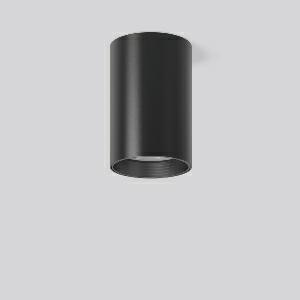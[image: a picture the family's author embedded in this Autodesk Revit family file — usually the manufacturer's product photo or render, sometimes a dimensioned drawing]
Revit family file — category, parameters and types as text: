
# Revit family: heledon_maxi_a_931227_003_1_ba15
name_source: partatom
category: Lighting Fixtures
units: mm (PartAtom-declared; Revit-internal decimal feet)

## family parameters
Cut with Voids When Loaded = No
Host = Face
Light Source = No
Part Type = Normal
Room Calculation Point = No
Round Connector Dimension = Use Diameter
Shared = No

## types (1)
- HELEDON maxi A (1 x LED Modul 940, 3900 lm, 4000)
    Apparent Load = 35 VA
    Approval mark = CE
    CIE Flux Codes = 97 100 100 100 100
    Color Rendering = 92
    Color Temperature = 4000
    Default Elevation = 1800 mm
    Description = Series: HELEDON maxi
Cylindrical surface-mounted downlight. Housing: die-cast aluminium, powder-coated. Internal ceiling frame polycarbonate with bayonet mounting. Black plastic ring and recessed LED to prevent glare from the side. Optical assembly with lens made of plastic (polycarbonate) for the best homogeneous light distribution - can be changed without tools. Best colour rendering index Ra>90. Suitable for Ceiling mounting. Easy installation with a separate ceiling frame with bayonet mounting and plug connection. Driver integrated. Connected via plug-in connector. High quality converter without flickering and stroboscopic effect. The following accessories can be mounted without use of tools: interchangeable lenses, decorative glasses, honeycomb louvre, clear and frosted diffusers, white interchangeable plastic ring. 
Colour: deep black, matt (RAL 9005)
Diameter: 123 mm
Height: 183 mm
Lamp: LED
Socket: without socket
Colour temperature: 4000K
Colour rendering index (CRI): 92
System power: 35 W
Rated luminous flux: 3900 lm
Luminous efficiency: 111 lm/W
Control gear: Regulated power supply
Protection class: I
Type of protection: IP 20
    Height = 183 mm
    Lamp = 1 x LED Modul 940
    Lamp Light Flux = 3900 lm
    Lamp count = 1
    Length = 123 mm
    Lifetime = 50000 h
    Luminous efficacy = 111 lm/W
    Manufacturer = RZB
    ModVariant = No
    Model = 931227.003.1
    Mounting Place = Ceiling
    Mounting Type = Surface mounted
    Number of Poles = 1
    OnlyDefault = Yes
    Power Factor = 1
    Product Name = HELEDON maxi A
    Product group = Surface mounted downlights
    ProductGroupID = 302
    Protection Class = Protection class I
    Protection Degree = IP 20
    RLX_Detail_Level = 1
    RLX_Emergency_Light_Flux = 0 lm
    RLX_Emergency_Type = 0
    RLX_Emergency_Type_DB = No
    RlxData = <blob elided: 97169 chars, md5=f080af1d>
    Socket = socket
    Standby Power = 0 W
    System Light Flux = 3900 lm
    System Power = 35 W
    Type Comments = Product without accessories
    Type Image = 931193.003.jpg
    URL = http://relux.com
    VarID = ---
    Voltage = 230 V
    Voltage Range = 220-240 V
    Weight = 0.00 kg
    Width = 0 mm  [stored 0 ft]

note: [stored X ft] marks values corroborated as IEEE doubles in the binary element streams (Revit-internal decimal feet)

## geometry (parser evidence)
native form markers: Blend x4, Sweep x8
no freeform markers — native parametric forms only
